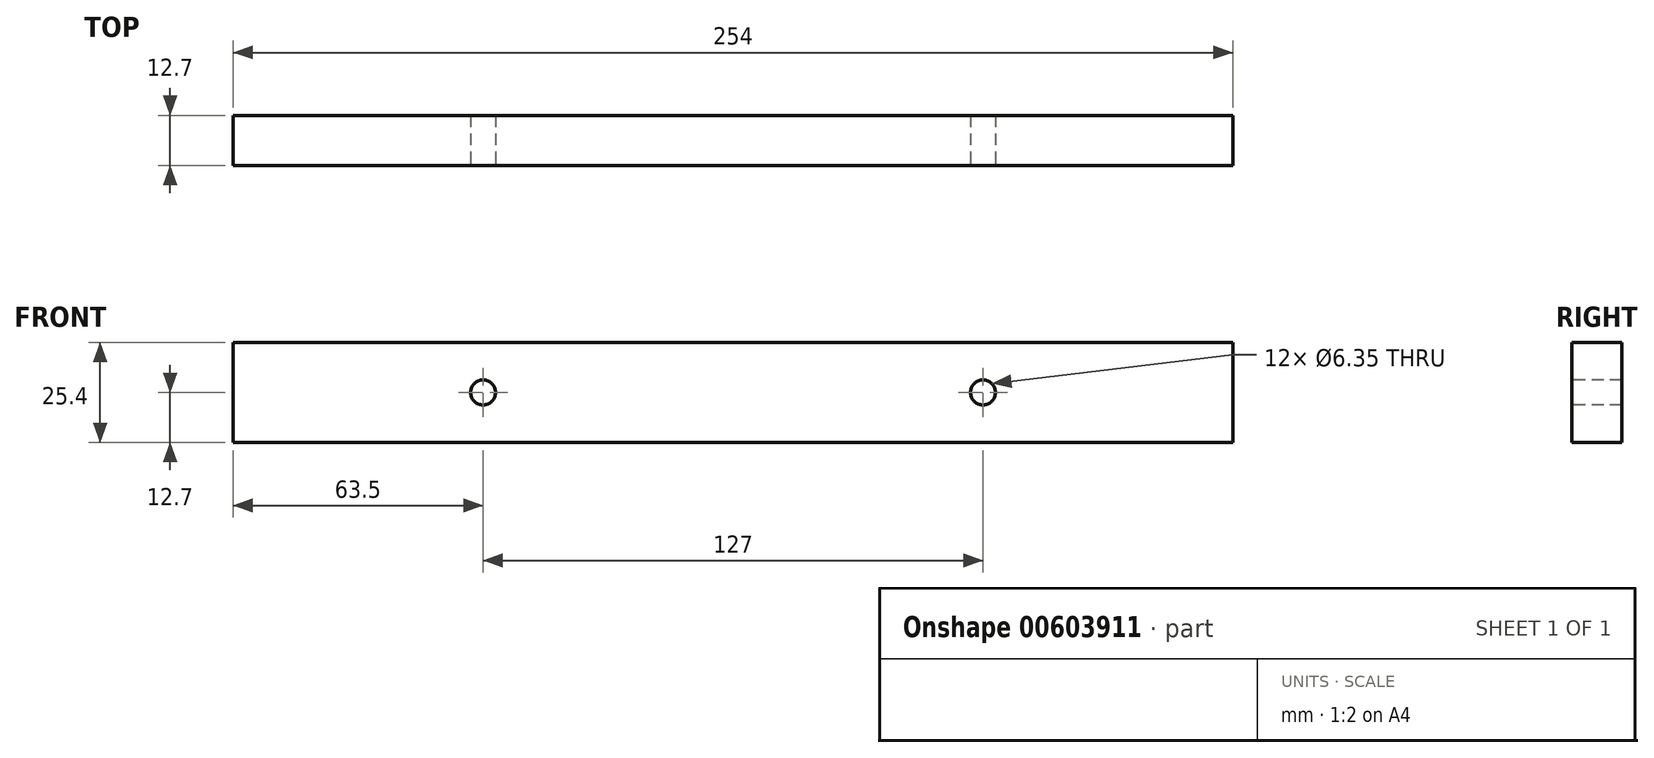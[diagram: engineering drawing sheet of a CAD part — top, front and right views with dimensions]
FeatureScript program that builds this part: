
annotation { "Feature Type Name" : "Feature", "Feature Type Description" : "" }
export const myFeature = defineFeature(function(context is Context, id is Id, definition is map)
    precondition{}
    {
        {
            var Q0;
            Q0=qCreatedBy(makeId("Right.planeOp"),FACE);
            var sketch = newSketch(context, id + "F0", { "sketchPlane" : qUnion([Q0])});
            skLineSegment(sketch, "E0.bottom", {"start": v(0, 0) * mm, "end": v(12.7, 0) * mm});
            skLineSegment(sketch, "E0.top", {"start": v(0, 25.4) * mm, "end": v(12.7, 25.4) * mm});
            skLineSegment(sketch, "E0.left", {"start": v(0, 0) * mm, "end": v(0, 25.4) * mm});
            skLineSegment(sketch, "E0.right", {"start": v(12.7, 0) * mm, "end": v(12.7, 25.4) * mm});
            skSolve(sketch);
        }
        {
            var Q0;
            Q0=makeQuery(id+"F0.imprint","IMPRINT",FACE,{"disambiguationData":[TD([[makeQuery(id+"F0.imprint","IMPRINT",EDGE,{"derivedFrom":sQuery(id+"F0.wireOp",EDGE,"E0.bottom")}),1.0]])]});
            extrude(context, id + "F1", {"entities" : qUnion([Q0]), "depth" : 127 * mm, "offsetDistance" : 25.4 * mm, "hasSecondDirection" : true, "secondDirectionOppositeDirection" : true, "secondDirectionDepth" : 127 * mm});
        }
        {
            var Q0;
            Q0=makeQuery(id+"F1.opExtrude","SWEPT_FACE",FACE,{"disambiguationData":[OSD([sQuery(id+"F0.wireOp",EDGE,"E0.left")])]});
            var sketch = newSketch(context, id + "F2", { "sketchPlane" : qUnion([Q0])});
            skPoint(sketch, "E1", {"position": v(-63.5, 12.7) * mm});
            skPoint(sketch, "E1.positionSnap0", {"position": v(-127, 12.7) * mm});
            skPoint(sketch, "E2", {"position": v(63.5, 12.7) * mm});
            skPoint(sketch, "E2.positionSnap0", {"position": v(127, 12.7) * mm});
            skSolve(sketch);
        }
        {
            var Q0;
            Q0=sQuery(id+"F2.wireOp",VERTEX,"E1");
            var Q1;
            Q1=sQuery(id+"F2.wireOp",VERTEX,"E2");
            var Q2;
            Q2=makeQuery(id+"F1.opExtrude","SWEPT_BODY",BODY,{"disambiguationData":[OSD([sQuery(id+"F0.wireOp",EDGE,"E0.bottom"),sQuery(id+"F0.wireOp",EDGE,"E0.top"),sQuery(id+"F0.wireOp",EDGE,"E0.left"),sQuery(id+"F0.wireOp",EDGE,"E0.right")])]});
            hole(context, id + "F3", {"style" : HoleStyle.SIMPLE, "endStyle" : HoleEndStyle.THROUGH, "holeDiameter" : 6.35 * mm, "majorDiameter" : 6.35 * mm, "isTappedThrough" : true, "tappedDepth" : 12.7 * mm, "tapClearance" : 3, "startFromSketch" : true, "locations" : qUnion([Q0, Q1]), "scope" : qUnion([Q2])});
        }
    });
